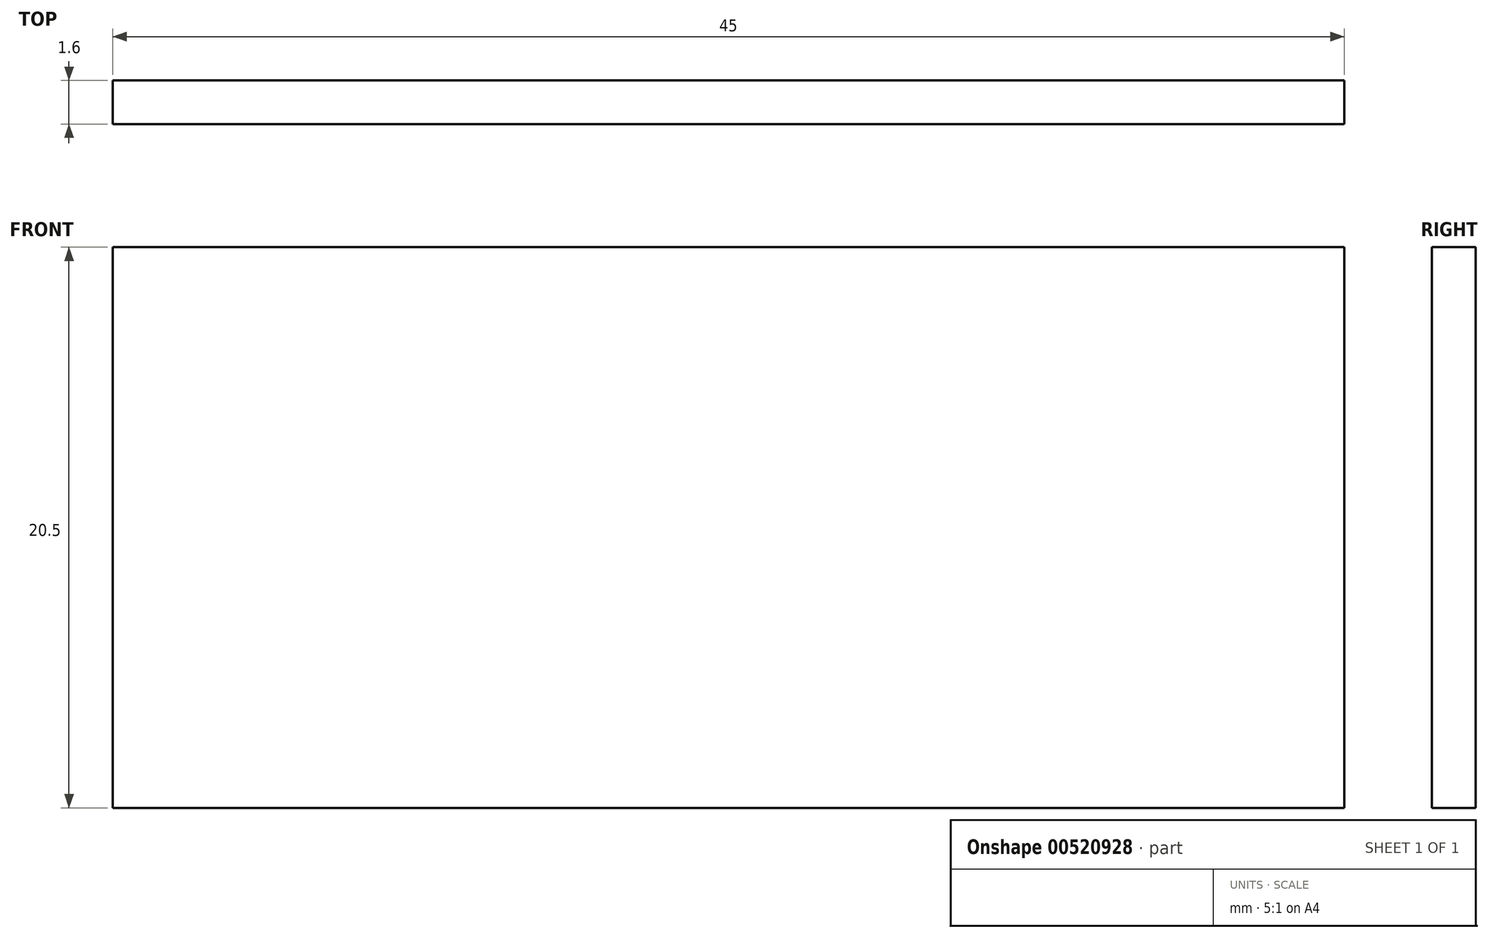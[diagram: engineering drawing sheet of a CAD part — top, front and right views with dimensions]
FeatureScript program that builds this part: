
annotation { "Feature Type Name" : "Feature", "Feature Type Description" : "" }
export const myFeature = defineFeature(function(context is Context, id is Id, definition is map)
    precondition{}
    {
        {
            var Q0;
            Q0=qCreatedBy(makeId("Front.planeOp"),FACE);
            var sketch = newSketch(context, id + "F0", { "sketchPlane" : qUnion([Q0])});
            skLineSegment(sketch, "E0.bottom", {"start": v(-22.5, 10.25) * mm, "end": v(22.5, 10.25) * mm});
            skLineSegment(sketch, "E0.top", {"start": v(-22.5, -10.25) * mm, "end": v(22.5, -10.25) * mm});
            skLineSegment(sketch, "E0.left", {"start": v(-22.5, 10.25) * mm, "end": v(-22.5, -10.25) * mm});
            skLineSegment(sketch, "E0.right", {"start": v(22.5, 10.25) * mm, "end": v(22.5, -10.25) * mm});
            skPoint(sketch, "E0.middle", {"position": v(0, 0) * mm});
            skSolve(sketch);
        }
        {
            var Q0;
            Q0=makeQuery(id+"F0.imprint","IMPRINT",FACE,{"disambiguationData":[TD([[makeQuery(id+"F0.imprint","IMPRINT",EDGE,{"derivedFrom":sQuery(id+"F0.wireOp",EDGE,"E0.bottom")}),-1.0]])]});
            extrude(context, id + "F1", {"entities" : qUnion([Q0]), "depth" : 1.6 * mm, "offsetDistance" : 25.4 * mm});
        }
        {
            var Q0;
            Q0=makeQuery(id+"F1.opExtrude","CAP_FACE",FACE,{"disambiguationData":[OSD([sQuery(id+"F0.wireOp",EDGE,"E0.bottom"),sQuery(id+"F0.wireOp",EDGE,"E0.top"),sQuery(id+"F0.wireOp",EDGE,"E0.left"),sQuery(id+"F0.wireOp",EDGE,"E0.right")])],"isStart":false});
            var sketch = newSketch(context, id + "F2", { "sketchPlane" : qUnion([Q0])});
            skCircle(sketch, "E1", {"center": v(-12.95, 0) * mm, "radius": 8 * mm});
            skCircle(sketch, "E2", {"center": v(12.05, 0) * mm, "radius": 8 * mm});
            skSolve(sketch);
        }
        {
            var Q0;
            Q0=sQuery(id+"F2.wireOp",EDGE,"E1");
            var Q1;
            Q1=sQuery(id+"F2.wireOp",EDGE,"E2");
            extrude(context, id + "F3", {"bodyType" : ToolBodyType.SURFACE, "surfaceEntities" : qUnion([Q0, Q1]), "depth" : 5 * mm, "offsetDistance" : 25.4 * mm});
        }
    });
